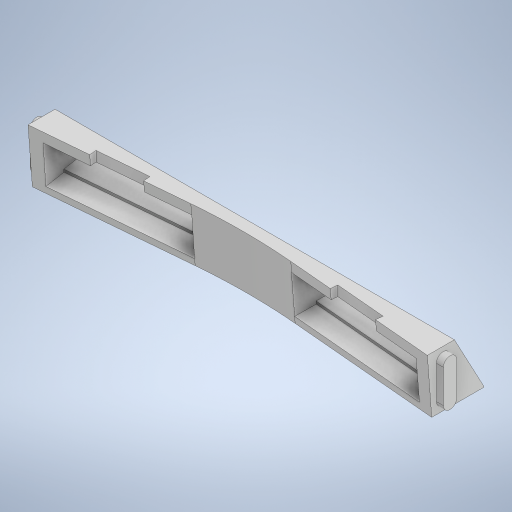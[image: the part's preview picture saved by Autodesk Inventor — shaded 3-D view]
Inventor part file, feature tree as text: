
AUTODESK INVENTOR PART (.ipt)
format: ipt  version: 2023 (Build 270158000, 158)  size: 509,952 bytes
history: native  units: mm
features: projected_geometry x18, extrude x16, sketch x16, other x14, reference x4, fillet x2, mirror x1
ambient origin geometry x8: Origin, YZ Plane, XZ Plane, XY Plane, X Axis, Y Axis, Z Axis, Center Point
bodies: Body1 (feature_tree)
feature tree (71):
  other  "Bryła1"
  extrude  "Wyciągnięcie proste1"  Depth=10.796607mm
  extrude  "Wyciągnięcie proste2"  Depth=10.0mm
  extrude  "Wyciągnięcie proste3"  Depth=2.5mm
  extrude  "Wyciągnięcie proste4"  Depth=25.0mm TaperAngle=0.0deg
  other  "Edytuj bezpośrednio1"
  extrude  "Wyciągnięcie proste7"  Depth=14.835299mm
  extrude  "Wyciągnięcie proste8"  Depth=14.835299mm
  extrude  "Wyciągnięcie proste9"  TaperAngle=0.0deg  [1 undecoded]
  extrude  "Wyciągnięcie proste10"  Depth=1.0mm TaperAngle=0.0deg
  sketch  "Szkic11"
  other  "Płaszczyzna konstrukcyjna1"
  extrude  "Wyciągnięcie proste11"  Depth=1.0mm TaperAngle=0.0deg
  extrude  "Wyciągnięcie proste12"  Depth=2.0mm TaperAngle=0.0deg
  extrude  "Wyciągnięcie proste13"  Depth=6.3mm
  extrude  "Wyciągnięcie proste14"  Depth=8.4mm
  extrude  "Wyciągnięcie proste15"  Depth=0.774926mm
  mirror  "Odbij3"
  other  "Edytuj bezpośrednio7"
  other  "Edytuj bezpośrednio8"
  extrude  "Wyciągnięcie proste16"  Depth=29.5mm TaperAngle=0.0deg
  extrude  "Wyciągnięcie proste17"  Depth=2.0mm TaperAngle=0.0deg
  extrude  "Wyciągnięcie proste18"  Depth=0.6mm TaperAngle=0.0deg
  fillet  "Zaokrąglenie1"  [1 undecoded]
  fillet  "Zaokrąglenie2"  Radius=0.3mm
  sketch  "Szkic1"
  sketch  "Szkic2"
  projected_geometry  "Pętla rzutowana1"
  projected_geometry  "Pętla rzutowana2"
  sketch  "Szkic3"
  projected_geometry  "Pętla rzutowana3"
  sketch  "Szkic4"
  projected_geometry  "Pętla rzutowana4"
  sketch  "Szkic7"
  sketch  "Szkic8"
  projected_geometry  "Pętla rzutowana7"
  projected_geometry  "Pętla rzutowana8"
  sketch  "Szkic9"
  projected_geometry  "Pętla rzutowana9"
  reference  "Odniesienie1"
  sketch  "Szkic10"
  projected_geometry  "Pętla rzutowana10"
  projected_geometry  "Pętla rzutowana11"
  reference  "Odniesienie2"
  reference  "Odniesienie3"
  sketch  "Szkic14"
  projected_geometry  "Pętla rzutowana14"
  sketch  "Szkic15"
  projected_geometry  "Pętla rzutowana15"
  projected_geometry  "Pętla rzutowana16"
  sketch  "Szkic16"
  projected_geometry  "Pętla rzutowana17"
  sketch  "Szkic17"
  projected_geometry  "Pętla rzutowana18"
  sketch  "Szkic18"
  projected_geometry  "Pętla rzutowana19"
  projected_geometry  "Pętla rzutowana20"
  reference  "Odniesienie4"
  sketch  "Szkic19"
  projected_geometry  "Pętla rzutowana21"
  sketch  "Szkic20"
  projected_geometry  "Pętla rzutowana22"
  other  "Przesuń1"
  other  "<userpath>\Desktop\MojeRoboty\Stefan\mechanics 2\STEFAN.iam"
  other  "STEFAN.iam"
  other  "GP2Y0A41SK0F:2"
  other  "Przesuń8"
  other  "Przesuń9"
  other  "Przesuń10"
  other  "Przesuń11"
  other  "sciana_awaryjna:1"
note: 2 required parameter values undecoded (feature->parameter linkage not recoverable at this tier; creation-order binding heuristic only, values carry confidence <= 0.55)
